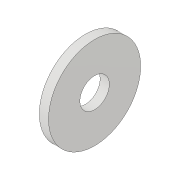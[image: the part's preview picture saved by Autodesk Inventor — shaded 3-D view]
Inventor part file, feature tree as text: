
AUTODESK INVENTOR PART (.ipt)
format: ipt  version: 2019.4 (Build 234330000, 330)  size: 79,872 bytes
history: native  units: mm
features: other x1, extrude x1, sketch x1
ambient origin geometry x8: Origin, YZ Plane, XZ Plane, XY Plane, X Axis, Y Axis, Z Axis, Center Point
bodies: Body1 (feature_tree)
feature tree (3):
  other  "ソリッド1"
  extrude  "押し出し1"  Depth=10.0mm
  sketch  "スケッチ1"
